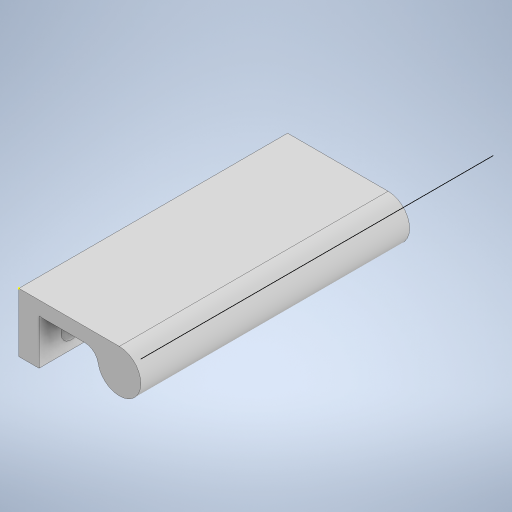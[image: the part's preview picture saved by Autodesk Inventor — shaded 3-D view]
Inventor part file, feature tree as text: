
AUTODESK INVENTOR PART (.ipt)
format: ipt  version: 2024.2 (Build 282272000, 272)  size: 268,800 bytes
history: native  units: in
note: dims shown in document units (in); Inventor stores cm internally (conversion verified against a paired STEP export)
features: sketch x4, extrude x3
ambient origin geometry x8: Origin, YZ Plane, XZ Plane, XY Plane, X Axis, Y Axis, Z Axis, Center Point
bodies: Solid1 (feature_tree)
feature tree (7):
  extrude  "Extrusion1"  Depth=0.55in
  extrude  "Extrusion2"  Depth=0.3937in
  extrude  "Extrusion3"  Depth=0.1875in TaperAngle=0.0deg
  sketch  "Sketch4"  dims[d14=0.13in d15=0.04in d16=0.0in d17=0.935in d18=0.4in d19=0.125in d20=2.5in d21=0.0in]
  sketch  "Sketch1"  dims[d0=2.5in d1=0.55in]
  sketch  "Sketch2"  dims[d3=0.375in d4=2.7559in d6=0.3149in d7=0.3937in d9=1.0in]
  sketch  "Sketch3"  dims[d11=0.3in d12=0.1875in d13=0.0in]
